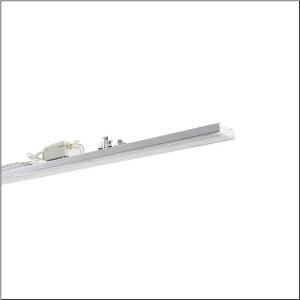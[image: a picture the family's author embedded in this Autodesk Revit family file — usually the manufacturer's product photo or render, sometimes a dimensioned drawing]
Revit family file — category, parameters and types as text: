
# Revit family: licross_r__21_recessed_mo_52tl18vn58xg_02ab
name_source: partatom
category: Lighting Fixtures
units: mm (PartAtom-declared; Revit-internal decimal feet)

## family parameters
Cut with Voids When Loaded = No
Host = Face
Light Source = No
Part Type = Normal
Room Calculation Point = No
Round Connector Dimension = Use Diameter
Shared = No

## types (1)
- --- (1 x LED, 8000 lm, 46.1 W, 5000K)
    Apparent Load = 46 VA
    CIE Flux Codes = 79 95 99 100 100
    Color Rendering = 80
    Color Temperature = 5000K
    Default Elevation = 1800 mm
    Description = Licross® 21 Recessed MO, luminaire insert, of sheet steel, galvanised, coil coated, white, length: 1.500mm, width: 66mm, height: 67mm, LED rated luminous flux: 8.000lm, light colour: 850, control gear: DALI 2, CLO, with plug, 5-pole, with phase selection, mains connection: 220..240V, AC, 50/60Hz, start of lifetime: 46W, end of service life: 55W, halogen-free wiring, primary optical cover: cover, of PMMA, light emission: direct distribution, primary light characteristic: symmetric, protection rating (complete): IP40, insulation class (complete): insulation class I (protective earthing), certification: CE, ENEC, VDE, UKCA, protection symbol: D if used in an environment without relevant dust loads with corresponding accessories, impact resistance: IK06, permissible ambient temperature for indoor applications: -25..+40°C, corresponds to IFS (International Featured Standards) requirements for safety and quality in the food industry, reducing of maximum allowable ambient temperature of 5°C with ceiling mounting, LABS conformity tested according to VDMA 24364:2018-05, packaging unit: 1 piece
    Height = 58 mm
    Lamp = 1 x LED
    Lamp Light Flux = 8000 lm
    Lamp Power = 46.1 W
    Lamp count = 1
    Length = 1500 mm
    Luminous efficacy = 174 lm/W
    Manufacturer = Siteco
    ModVariant = No
    Model = 52TL18VN58XG
    Mounting Place = Ceiling
    Mounting Type = Pendant
    Number of Poles = 1
    OnlyDefault = Yes
    Power Factor = 1
    Product Name = Licross® 21 Recessed MO
    Product group = luminaire insert
    ProductGroupID = 901
    Protection Class = Protection class I
    Protection Degree = IP 40
    RLX_Detail_Level = 1
    RLX_Emergency_Light_Flux = 0 lm
    RLX_Emergency_Type = 0
    RLX_Emergency_Type_DB = No
    RlxData = <blob elided: 24577 chars, md5=554abf33>
    Socket = socket
    Standby Power = 0 W
    System Light Flux = 8000 lm
    System Power = 46 W
    Type Comments = factory setting: luminous flux: 100 % | dim-lin: 254 | 310 mA
    Type Image = l_1296930.jpg
    URL = http://relux.com
    VarID = @adj_051353
    Voltage = 0 V
    Weight = 0.00 kg
    Width = 66 mm

## geometry (parser evidence)
native form markers: Blend x4, Sweep x12
no freeform markers — native parametric forms only
